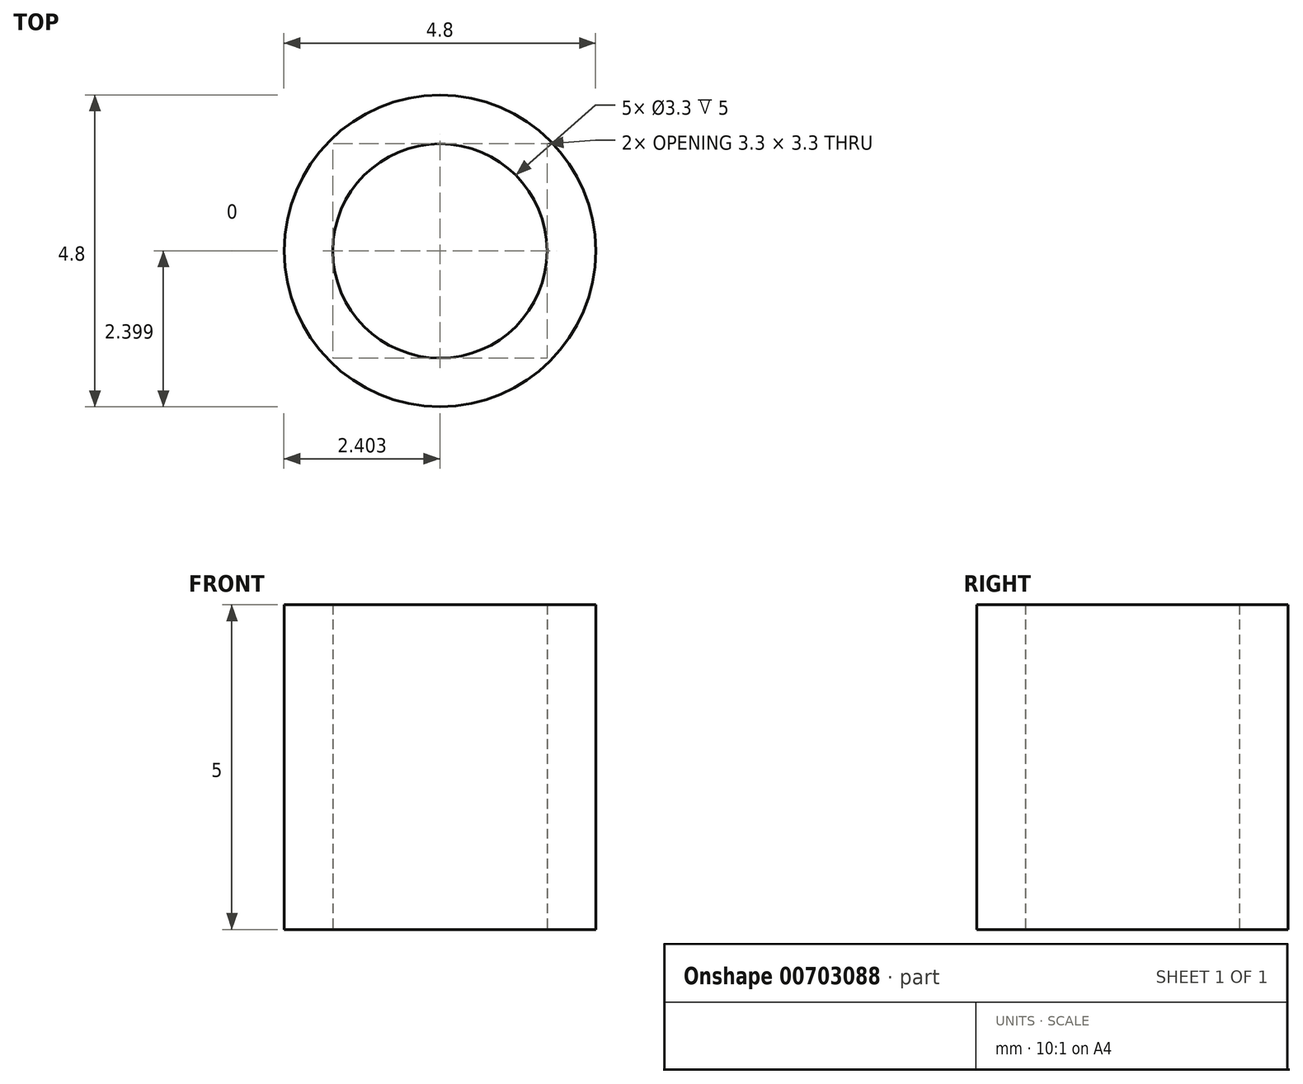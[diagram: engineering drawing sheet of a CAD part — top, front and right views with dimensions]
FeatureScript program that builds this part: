
annotation { "Feature Type Name" : "Feature", "Feature Type Description" : "" }
export const myFeature = defineFeature(function(context is Context, id is Id, definition is map)
    precondition{}
    {
        {
            var Q0;
            Q0=qCreatedBy(makeId("Top.planeOp"),FACE);
            var sketch = newSketch(context, id + "F0", { "sketchPlane" : qUnion([Q0])});
            skCircle(sketch, "E0", {"center": v(-17.3, 13.92) * mm, "radius": 2.4 * mm});
            skSolve(sketch);
        }
        {
            var Q0;
            Q0=makeQuery(id+"F0.imprint","IMPRINT",FACE,{"disambiguationData":[TD([[makeQuery(id+"F0.imprint","IMPRINT",EDGE,{"derivedFrom":sQuery(id+"F0.wireOp",EDGE,"E0")}),1.0]])]});
            var Q1;
            Q1=sQuery(id+"F0.wireOp",EDGE,"E0");
            extrude(context, id + "F1", {"entities" : qUnion([Q0]), "surfaceEntities" : qUnion([Q1]), "depth" : 5 * mm, "offsetDistance" : 25 * mm});
        }
        {
            var Q0;
            Q0=sQuery(id+"F0.wireOp",VERTEX,"E0.center");
            var Q1;
            Q1=makeQuery(id+"F1.opExtrude","SWEPT_BODY",BODY,{"disambiguationData":[OSD([sQuery(id+"F0.wireOp",EDGE,"E0")])]});
            hole(context, id + "F2", {"style" : HoleStyle.SIMPLE, "endStyle" : HoleEndStyle.THROUGH, "oppositeDirection" : true, "standardTappedOrClearance" : lookupTablePath({ "standard" : "ISO", "fit" : "Normal", "size" : "M3", "type" : "Clearance" }), "standardBlindInLast" : lookupTablePath({ "fit" : "Standard", "standard" : "ISO", "size" : "M3", "type" : "Clearance" }), "holeDiameter" : 3.3 * mm, "majorDiameter" : 5 * mm, "isTappedThrough" : true, "tappedDepth" : 12 * mm, "tapClearance" : 3, "locations" : qUnion([Q0]), "scope" : qUnion([Q1])});
        }
    });
